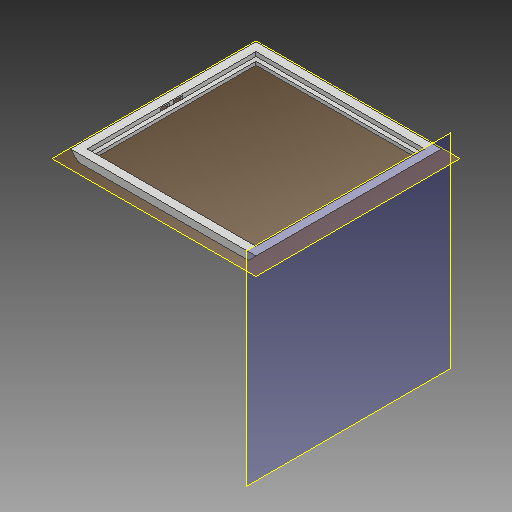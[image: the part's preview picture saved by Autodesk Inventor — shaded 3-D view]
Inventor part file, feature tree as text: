
AUTODESK INVENTOR PART (.ipt)
format: ipt  version: 2018.3 (Build 223284000, 284)  size: 206,848 bytes
history: native  units: mm
features: reference x20, other x12, extrude x6, sketch x6, plane x2, chamfer x1, projected_geometry x1
ambient origin geometry x8: Origin, YZ Plane, XZ Plane, XY Plane, X Axis, Y Axis, Z Axis, Center Point
bodies: Volumenkörper1 (feature_tree)
feature tree (48):
  extrude  "Extrusion1"  [1 undecoded]
  plane  "Arbeitsebene1"
  extrude  "Extrusion2"  Depth=10.0mm
  extrude  "Extrusion3"  Depth=10.0mm
  plane  "Arbeitsebene3"
  extrude  "Extrusion4"  Depth=8.0mm TaperAngle=0.0deg
  extrude  "Extrusion5"  Depth=2.0mm TaperAngle=0.0deg
  extrude  "Extrusion6"  Depth=18.0mm TaperAngle=45.0deg
  chamfer  "Fase2"  [1 undecoded]
  sketch  "Skizze1"  dims[d0=18.0mm d1=0.0mm d5=-20.0mm]
  reference  "Referenz1"
  reference  "Referenz2"
  reference  "Referenz3"
  reference  "Referenz4"
  reference  "Referenz5"
  sketch  "Skizze3"  dims[d6=17.0mm d7=0.0mm d8=10.0mm]
  reference  "Referenz12"
  reference  "Referenz13"
  reference  "Referenz14"
  reference  "Referenz15"
  reference  "Referenz16"
  reference  "Referenz17"
  reference  "Referenz18"
  reference  "Referenz19"
  sketch  "Skizze5"  dims[d9=10.0mm d10=10.0mm]
  sketch  "Skizze6"  dims[d11=10.0mm d12=8.0mm d13=0.0mm]
  reference  "Referenz20"
  reference  "Referenz21"
  reference  "Referenz22"
  reference  "Referenz23"
  reference  "Referenz24"
  reference  "Referenz25"
  sketch  "Skizze7"  dims[d14=25.0mm d15=0.0mm d16=2.0mm d17=0.0mm]
  projected_geometry  "Projizierte Kontur1"
  sketch  "Skizze8"  dims[d18=2.0mm d19=0.0mm d20=18.0mm d21=2.0mm d22=45.0deg]
  reference  "Referenz26"
  parser-record x2  (decoder bookkeeping rows leaked as tree rows — omitted from the tree; the rows remain in map.json)
  other  "SmartCube_Quadratisch.iam"
  other  "Wand2_MIR:1"
  other  "Wand1:1"
  other  "Wand1_MIR:1"
  other  "Wand2:1"
  other  "PV_Modul:1"
  other  "<userpath>\Documents\Dipl\Smartcube_Construction\Version_3\Baugruppe1.iam"
  other  "Baugruppe1.iam"
  other  "PV_Ramen_CPY_3_2:1"
  other  "PV_Modul_CPY_3_CPY1:1"
note: 2 required parameter values undecoded (feature->parameter linkage not recoverable at this tier; creation-order binding heuristic only, values carry confidence <= 0.55)
note: 2 file-system paths scrubbed to <path> (originals preserved in map.json)
